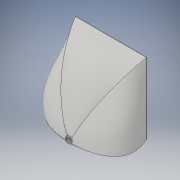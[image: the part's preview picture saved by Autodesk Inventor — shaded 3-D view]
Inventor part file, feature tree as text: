
AUTODESK INVENTOR PART (.ipt)
format: ipt  version: 2017 (Build 210142000, 142)  size: 411,648 bytes
history: native  units: in
note: dims shown in document units (in); Inventor stores cm internally (conversion verified against a paired STEP export)
features: sketch x4, extrude x2, other x2, loft x2
ambient origin geometry x8: Origin, YZ Plane, XZ Plane, XY Plane, X Axis, Y Axis, Z Axis, Center Point
bodies: Solid1 (feature_tree)
feature tree (10):
  extrude  "connection"  Depth=1.0in
  other  "front half of room"
  sketch  "Sketch2"  dims[d17=30.0in d26=69.0in d27=59.0in d28=102.0in]
  other  "front of room"
  sketch  "Sketch3"  dims[d29=102.0in d33=1.0in d34=1.0in]
  loft  "shell make "
  loft  "shell cut"
  extrude  "connection to door"  Depth=1.0in
  sketch  "Sketch1"  dims[d12=1.0in d13=0.0in d14=30.0in]
  sketch  "Sketch5"  dims[d35=1.0in d36=1.0in d55=100.0in d56=100.0in d57=1.0in d58=0.0in d82=4.0in d83=1.0in d84=4.8944in d85=0.5833in d86=3.8873in d87=3.8873in d88=1.7083in d89=0.0625in d90=0.0625in d91=1.6458in d92=0.125in d93=0.125in d151=70.0in d152=60.0in d153=69.0in d154=59.0in d157=0.0in d158=90.0deg d159=0.0in d160=90.0deg d161=0.0in d162=90.0deg d179=1.0in d180=0.0in d181=90.0deg d182=0.0in d183=90.0deg d184=0.0in d185=90.0deg d217=54.4672in]
